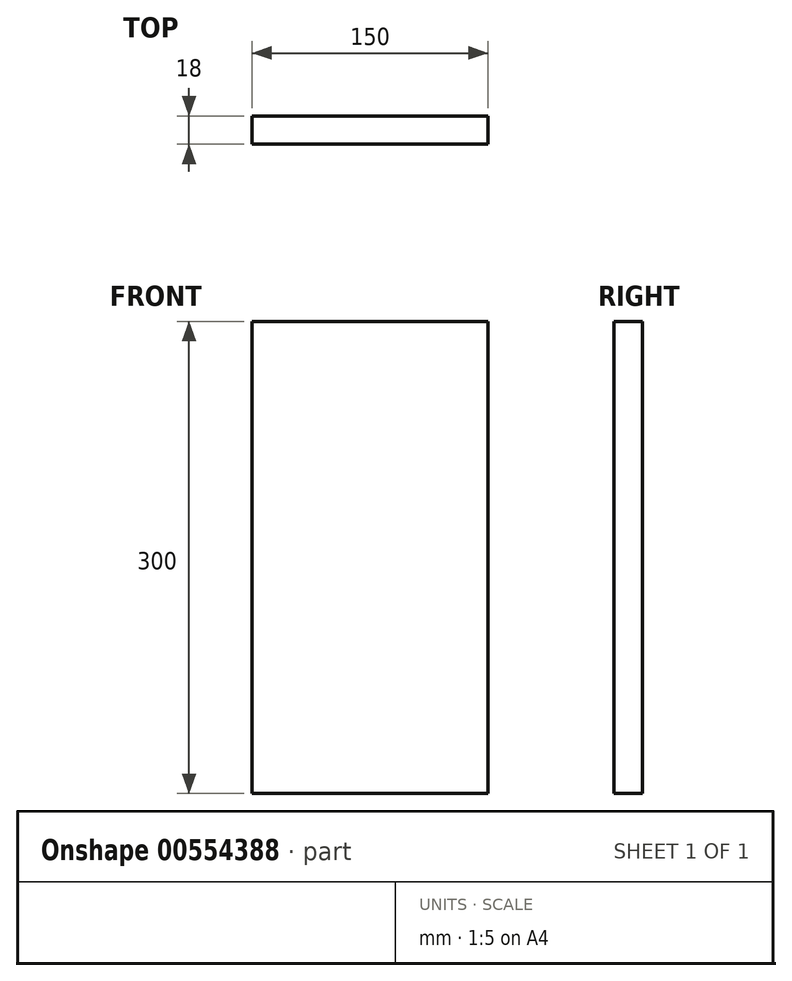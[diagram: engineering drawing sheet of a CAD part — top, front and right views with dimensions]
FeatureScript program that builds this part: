
annotation { "Feature Type Name" : "Feature", "Feature Type Description" : "" }
export const myFeature = defineFeature(function(context is Context, id is Id, definition is map)
    precondition{}
    {
        {
            var Q0;
            Q0=qCreatedBy(makeId("Front.planeOp"),FACE);
            var sketch = newSketch(context, id + "F0", { "sketchPlane" : qUnion([Q0])});
            skLineSegment(sketch, "E0.bottom", {"start": v(0, 0) * mm, "end": v(150, 0) * mm});
            skLineSegment(sketch, "E0.top", {"start": v(0, 300) * mm, "end": v(150, 300) * mm});
            skLineSegment(sketch, "E0.left", {"start": v(0, 0) * mm, "end": v(0, 300) * mm});
            skLineSegment(sketch, "E0.right", {"start": v(150, 0) * mm, "end": v(150, 300) * mm});
            skSolve(sketch);
        }
        {
            var Q0;
            Q0=makeQuery(id+"F0.imprint","IMPRINT",FACE,{"disambiguationData":[TD([[makeQuery(id+"F0.imprint","IMPRINT",EDGE,{"derivedFrom":sQuery(id+"F0.wireOp",EDGE,"E0.bottom")}),1.0]])]});
            extrude(context, id + "F1", {"entities" : qUnion([Q0]), "depth" : 18 * mm, "offsetDistance" : 25 * mm});
        }
    });
